# Revit family: sh-4501
name_source: partatom
category: Lighting Fixtures
revit_build: Autodesk Revit 2017 (Build: 20160225_1515(x64)
units: mm (PartAtom-declared; Revit-internal decimal feet)

## family parameters
Always vertical = Yes
Cut with Voids When Loaded = No
Host = Wall
Light Source = Yes
OmniClass Number = 23.80.70.00
OmniClass Title = Lighting
Part Type = Normal
Room Calculation Point = No
Round Connector Dimension = Use Diameter
Shared = Yes

## types (2) — shared parameters
Body Material = Aluminum
Color Filter = 16777215
Diffuser = Diffuser
Diffuser Material = polycarbonate-anti uv
Dimming Lamp Color Temperature Shift = <None>
Emit Shape Visible in Rendering = No
Emit from Circle Diameter = 61.0 cm
Height = 35.9 cm
IP = X3
Lamp = E27
Manufacturer = SHOA
Model = SH-4501
Photometric Web File = 4376_V-TAC7WLEDBulbE27A60Thermoplastic3000K_1-5117.ies
Protection Class = class I
Tilt Angle = 90.00°
URL = https://www.shoaco.com
Voltage/Frequency = 230 V Ac/50HZ
Website = www.shoaco.com
consumption current = 0 A
instalation = Wall Mounted
zero-valued in all types: Cost

## per-type parameters (varying)
| type | Body color | wattage. |
| SH-4501(Black body-3000K-E27) | Black Body | 9 W |
| SH-4501(White body-E27) | white body | 0 W |

## geometry (parser evidence)
native form markers: Sweep x4
no freeform markers — native parametric forms only
